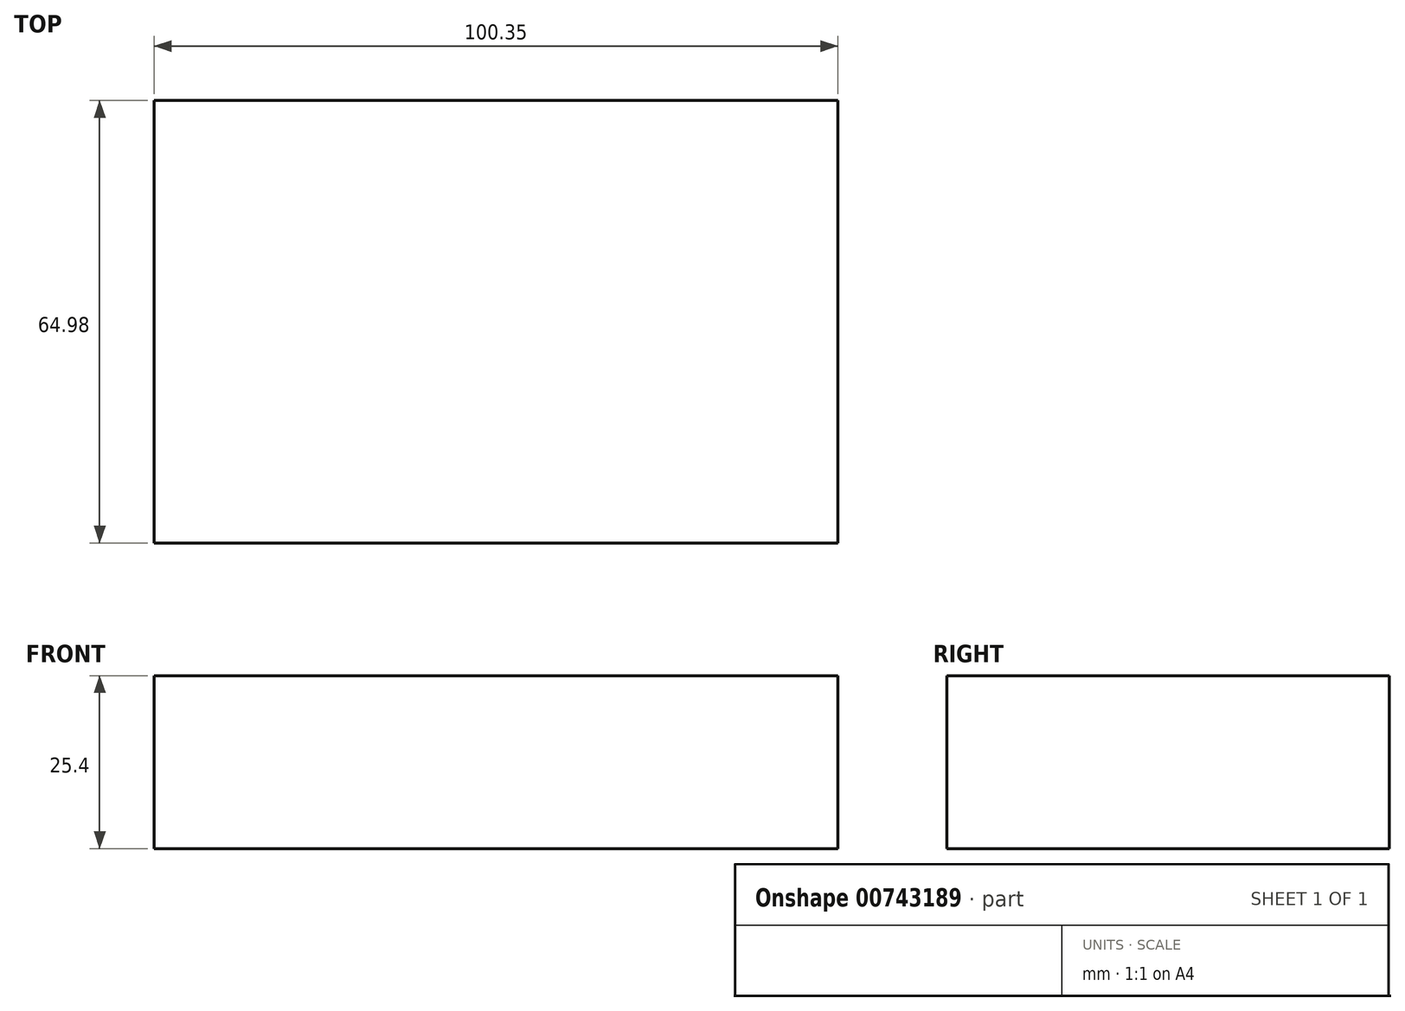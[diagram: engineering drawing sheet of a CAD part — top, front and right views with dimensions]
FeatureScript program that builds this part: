
annotation { "Feature Type Name" : "Feature", "Feature Type Description" : "" }
export const myFeature = defineFeature(function(context is Context, id is Id, definition is map)
    precondition{}
    {
        {
            var Q0;
            Q0=qCreatedBy(makeId("Top.planeOp"),FACE);
            var sketch = newSketch(context, id + "F0", { "sketchPlane" : qUnion([Q0])});
            skLineSegment(sketch, "E0.bottom", {"start": v(-52.77, 32.28) * mm, "end": v(47.58, 32.28) * mm});
            skLineSegment(sketch, "E0.top", {"start": v(-52.77, -32.7) * mm, "end": v(47.58, -32.7) * mm});
            skLineSegment(sketch, "E0.left", {"start": v(-52.77, 32.28) * mm, "end": v(-52.77, -32.7) * mm});
            skLineSegment(sketch, "E0.right", {"start": v(47.58, 32.28) * mm, "end": v(47.58, -32.7) * mm});
            skSolve(sketch);
        }
        {
            var Q0;
            Q0=makeQuery(id+"F0.imprint","IMPRINT",FACE,{"disambiguationData":[TD([[makeQuery(id+"F0.imprint","IMPRINT",EDGE,{"derivedFrom":sQuery(id+"F0.wireOp",EDGE,"E0.bottom")}),-1.0]])]});
            extrude(context, id + "F1", {"entities" : qUnion([Q0]), "depth" : 25.4 * mm, "offsetDistance" : 25.4 * mm});
        }
    });
